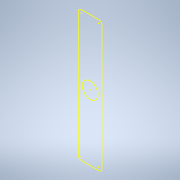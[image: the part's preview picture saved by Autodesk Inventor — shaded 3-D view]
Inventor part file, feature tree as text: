
AUTODESK INVENTOR PART (.ipt)
format: ipt  version: 2022 (Build 260153000, 153)  size: 86,528 bytes
history: native  units: mm
features: other x3, sketch x1, reference x1
ambient origin geometry x8: Origin, YZ Plane, XZ Plane, XY Plane, X Axis, Y Axis, Z Axis, Center Point
feature tree (5):
  sketch  "Sketch1"
  reference  "Reference1"
  other  "<userpath>\OneDrive\Namizje\school\3. letnik\ZOPp\laserski merilnik\3d model\Assembly1.iam"
  other  "Assembly1.iam"
  other  "constraining plate:1"
